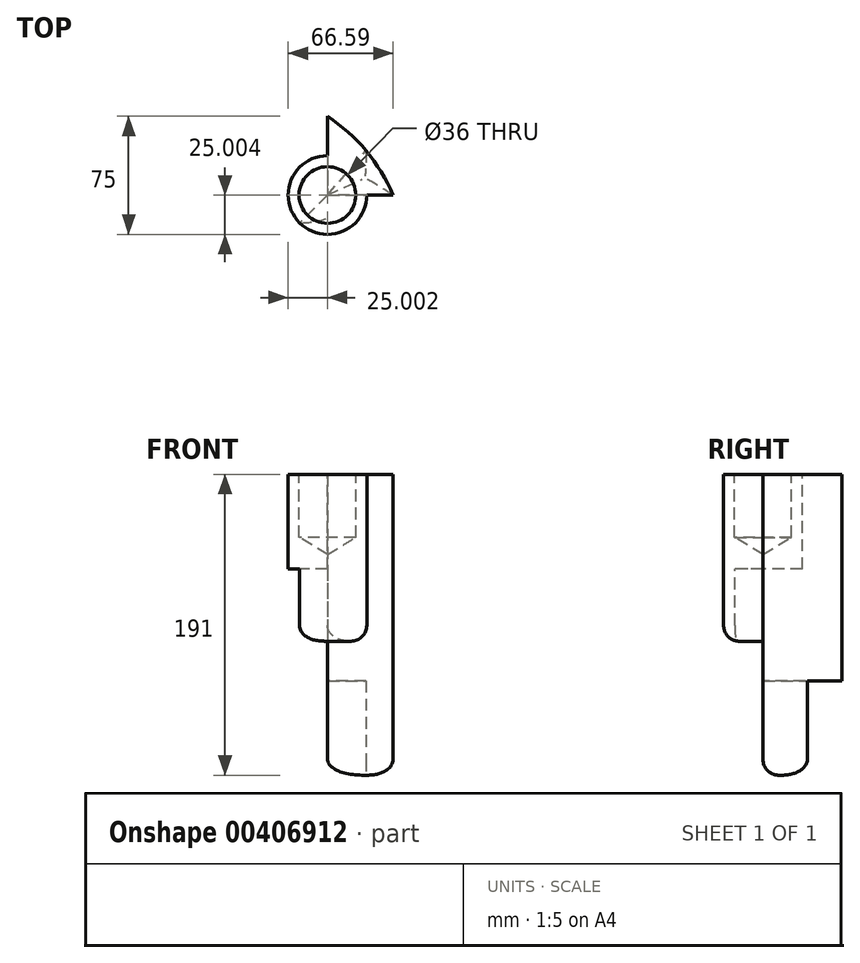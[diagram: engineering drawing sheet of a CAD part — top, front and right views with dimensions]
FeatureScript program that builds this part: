
annotation { "Feature Type Name" : "Feature", "Feature Type Description" : "" }
export const myFeature = defineFeature(function(context is Context, id is Id, definition is map)
    precondition{}
    {
        {
            var Q0;
            Q0=qCreatedBy(makeId("Top.planeOp"),FACE);
            var sketch = newSketch(context, id + "F0", { "sketchPlane" : qUnion([Q0])});
            skLineSegment(sketch, "E0.bottom", {"start": v(-15.97, 19) * mm, "end": v(34.03, 19) * mm});
            skLineSegment(sketch, "E0.top", {"start": v(-15.97, -31) * mm, "end": v(34.03, -31) * mm});
            skLineSegment(sketch, "E0.left", {"start": v(-15.97, 19) * mm, "end": v(-15.97, -31) * mm});
            skLineSegment(sketch, "E0.right", {"start": v(34.03, 19) * mm, "end": v(34.03, -31) * mm});
            skSolve(sketch);
        }
        {
            var Q0;
            Q0=makeQuery(id+"F0.imprint","IMPRINT",FACE,{"disambiguationData":[TD([[makeQuery(id+"F0.imprint","IMPRINT",EDGE,{"derivedFrom":sQuery(id+"F0.wireOp",EDGE,"E0.bottom")}),-1.0]])]});
            extrude(context, id + "F1", {"entities" : qUnion([Q0]), "depth" : 160 * mm});
        }
        {
            var Q0;
            Q0=makeQuery(id+"F1.opExtrude","SWEPT_BODY",BODY,{"disambiguationData":[OSD([sQuery(id+"F0.wireOp",EDGE,"E0.bottom"),sQuery(id+"F0.wireOp",EDGE,"E0.top"),sQuery(id+"F0.wireOp",EDGE,"E0.left"),sQuery(id+"F0.wireOp",EDGE,"E0.right")])]});
            var Q1;
            Q1=makeQuery(id+"F1.opExtrude","SWEPT_EDGE",EDGE,{"disambiguationData":[OSD([sQuery(id+"F0.wireOp",EDGE,"E0.bottom"),sQuery(id+"F0.wireOp",EDGE,"E0.left")])]});
            transform(context, id + "F2", {"entities" : qUnion([Q0]), "transformType" : TransformType.TRANSLATION_3D, "dx" : 20 * mm, "dy" : 22 * mm, "dz" : 0 * mm, "makeCopy" : false});
        }
        {
            var Q0;
            Q0=makeQuery(id+"F1.opExtrude","SWEPT_FACE",FACE,{"disambiguationData":[OSD([sQuery(id+"F0.wireOp",EDGE,"E0.top")])]});
            var sketch = newSketch(context, id + "F3", { "sketchPlane" : qUnion([Q0])});
            skLineSegment(sketch, "E1", {"start": v(4.03, 82.89) * mm, "end": v(29.03, 82.89) * mm});
            skLineSegment(sketch, "E2", {"start": v(29.03, 82.89) * mm, "end": v(29.03, 160) * mm});
            skLineSegment(sketch, "E3", {"start": v(29.03, 160) * mm, "end": v(4.03, 160) * mm});
            skLineSegment(sketch, "E4", {"start": v(4.03, 160) * mm, "end": v(4.03, 82.89) * mm});
            skSolve(sketch);
        }
        {
            var Q0;
            Q0 = qSketchRegion(id + "F3", true);
            var Q1;
            Q1=sQuery(id+"F3.wireOp",EDGE,"E4");
            revolve(context, id + "F4", {"operationType" : NewBodyOperationType.ADD, "entities" : qUnion([Q0]), "axis" : qUnion([Q1]), "revolveType" : RevolveType.FULL});
        }
        {
            var Q0;
            Q0=makeQuery(id+"F4.opRevolve","SWEPT_FACE",FACE,{"disambiguationData":[OSD([sQuery(id+"F3.wireOp",EDGE,"E1")])]});
            var sketch = newSketch(context, id + "F5", { "sketchPlane" : qUnion([Q0])});
            skLineSegment(sketch, "E5", {"start": v(4.03, 9) * mm, "end": v(-13.65, 26.67) * mm});
            skSolve(sketch);
        }
        {
            var Q0;
            Q0 = qSketchRegion(id + "F5", true);
            var Q1;
            {var subQ0=sQuery(id+"F5.wireOp",EDGE,"E5");Q1=makeQuery(id+"F5.imprint","IMPRINT",FACE,{"disambiguationData":[TD([[makeQuery(id+"F5.imprint","IMPRINT",EDGE,{"derivedFrom":subQ0}),-1.0]])]});}
            extrude(context, id + "F6", {"entities" : qUnion([Q0, Q1]), "operationType" : NewBodyOperationType.ADD, "depth" : 28.8 * mm});
        }
        {
            var Q0;
            Q0=makeQuery(id+"F4.opRevolve","SWEPT_FACE",FACE,{"disambiguationData":[OSD([sQuery(id+"F3.wireOp",EDGE,"E1")])]});
            extrude(context, id + "F7", {"entities" : qUnion([Q0]), "operationType" : NewBodyOperationType.REMOVE, "oppositeDirection" : true, "depth" : 17 * mm});
        }
        {
            var Q0;
            Q0=makeQuery(id+"F1.opExtrude","SWEPT_EDGE",EDGE,{"disambiguationData":[OSD([sQuery(id+"F0.wireOp",EDGE,"E0.bottom"),sQuery(id+"F0.wireOp",EDGE,"E0.right")])]});
            fillet(context, id + "F8", {"entities" : qUnion([Q0]), "radius" : 110 * mm, "tangentPropagation" : true, "allowEdgeOverflow" : false});
        }
        {
            var Q0;
            Q0=makeQuery(id+"F1.opExtrude","CAP_FACE",FACE,{"disambiguationData":[OSD([sQuery(id+"F0.wireOp",EDGE,"E0.bottom"),sQuery(id+"F0.wireOp",EDGE,"E0.top"),sQuery(id+"F0.wireOp",EDGE,"E0.left"),sQuery(id+"F0.wireOp",EDGE,"E0.right")])],"isStart":true});
            var sketch = newSketch(context, id + "F9", { "sketchPlane" : qUnion([Q0])});
            skLineSegment(sketch, "E6", {"start": v(4.03, 9) * mm, "end": v(28.6, -19.15) * mm});
            skSolve(sketch);
        }
        {
            var Q0;
            Q0 = qSketchRegion(id + "F9", true);
            var Q1;
            {var subQ0=sQuery(id+"F9.wireOp",EDGE,"E6");Q1=makeQuery(id+"F9.imprint","IMPRINT",FACE,{"disambiguationData":[TD([[makeQuery(id+"F9.imprint","IMPRINT",EDGE,{"derivedFrom":subQ0}),-1.0]])]});}
            extrude(context, id + "F10", {"entities" : qUnion([Q0, Q1]), "operationType" : NewBodyOperationType.REMOVE, "oppositeDirection" : true, "depth" : 29 * mm});
        }
        {
            var Q0;
            Q0=makeQuery(id+"F1.opExtrude","CAP_FACE",FACE,{"disambiguationData":[OSD([sQuery(id+"F0.wireOp",EDGE,"E0.bottom"),sQuery(id+"F0.wireOp",EDGE,"E0.top"),sQuery(id+"F0.wireOp",EDGE,"E0.left"),sQuery(id+"F0.wireOp",EDGE,"E0.right")])],"isStart":true});
            extrude(context, id + "F11", {"entities" : qUnion([Q0]), "operationType" : NewBodyOperationType.ADD, "depth" : 31 * mm});
        }
        {
            var Q0;
            Q0=makeQuery(id+"F7.boolean.opBoolean","COPY",EDGE,{"derivedFrom":makeQuery(id+"F7.opExtrude","CAP_EDGE",EDGE,{"disambiguationData":[OSD([sQuery(id+"F3.wireOp",EDGE,"E1"),sQuery(id+"F3.wireOp",EDGE,"E2")])],"isStart":false})});
            var Q1;
            Q1=makeQuery(id+"F6.opExtrude","CAP_EDGE",EDGE,{"disambiguationData":[OSD([sQuery(id+"F3.wireOp",EDGE,"E1"),sQuery(id+"F3.wireOp",EDGE,"E2")])],"isStart":false});
            var Q2;
            Q2=makeQuery(id+"F10.boolean.opBoolean","COPY",EDGE,{"derivedFrom":makeQuery(id+"F10.opExtrude","CAP_EDGE",EDGE,{"disambiguationData":[OSD([sQuery(id+"F0.wireOp",EDGE,"E0.left")])],"isStart":false})});
            var Q3;
            Q3=makeQuery(id+"F11.opExtrude","CAP_EDGE",EDGE,{"disambiguationData":[OSD([sQuery(id+"F9.wireOp",EDGE,"E6")])],"isStart":false});
            var Q4;
            Q4=makeQuery(id+"F11.opExtrude","CAP_EDGE",EDGE,{"disambiguationData":[OSD([sQuery(id+"F0.wireOp",EDGE,"E0.top")])],"isStart":false});
            var Q5;
            Q5=makeQuery(id+"F11.opExtrude","CAP_EDGE",EDGE,{"disambiguationData":[OSD([sQuery(id+"F0.wireOp",EDGE,"E0.bottom"),sQuery(id+"F0.wireOp",EDGE,"E0.top"),sQuery(id+"F0.wireOp",EDGE,"E0.left"),sQuery(id+"F0.wireOp",EDGE,"E0.right")])],"isStart":false});
            var Q6;
            Q6=makeQuery(id+"F10.boolean.opBoolean","COPY",EDGE,{"derivedFrom":makeQuery(id+"F10.opExtrude","CAP_EDGE",EDGE,{"disambiguationData":[OSD([sQuery(id+"F0.wireOp",EDGE,"E0.bottom"),sQuery(id+"F0.wireOp",EDGE,"E0.top"),sQuery(id+"F0.wireOp",EDGE,"E0.left"),sQuery(id+"F0.wireOp",EDGE,"E0.right")])],"isStart":false})});
            var Q7;
            Q7=makeQuery(id+"F6.opExtrude","CAP_EDGE",EDGE,{"disambiguationData":[OSD([sQuery(id+"F5.wireOp",EDGE,"E5")])],"isStart":false});
            fillet(context, id + "F12", {"entities" : qUnion([Q0, Q1, Q2, Q3, Q4, Q5, Q6, Q7]), "radius" : 10 * mm, "tangentPropagation" : true, "allowEdgeOverflow" : false});
        }
        {
            var Q0;
            Q0=makeQuery(id+"F4.boolean.opBoolean","MERGE",FACE,{"derivedFrom":[makeQuery(id+"F1.opExtrude","CAP_FACE",FACE,{"disambiguationData":[OSD([sQuery(id+"F0.wireOp",EDGE,"E0.bottom"),sQuery(id+"F0.wireOp",EDGE,"E0.top"),sQuery(id+"F0.wireOp",EDGE,"E0.left"),sQuery(id+"F0.wireOp",EDGE,"E0.right")])],"isStart":false}),makeQuery(id+"F4.opRevolve","SWEPT_FACE",FACE,{"disambiguationData":[OSD([sQuery(id+"F3.wireOp",EDGE,"E3")])]})]});
            var sketch = newSketch(context, id + "F13", { "sketchPlane" : qUnion([Q0])});
            skCircle(sketch, "E7", {"center": v(4.03, -9) * mm, "radius": 18 * mm});
            skSolve(sketch);
        }
        {
            var Q0;
            Q0=sQuery(id+"F13.wireOp",VERTEX,"E7.center");
            var Q1;
            Q1=makeQuery(id+"F1.opExtrude","SWEPT_BODY",BODY,{"disambiguationData":[OSD([sQuery(id+"F0.wireOp",EDGE,"E0.bottom"),sQuery(id+"F0.wireOp",EDGE,"E0.top"),sQuery(id+"F0.wireOp",EDGE,"E0.left"),sQuery(id+"F0.wireOp",EDGE,"E0.right")])]});
            hole(context, id + "F14", {"style" : HoleStyle.SIMPLE, "endStyle" : HoleEndStyle.BLIND, "holeDiameter" : 36 * mm, "holeDepth" : 40 * mm, "isTappedThrough" : true, "tappedDepth" : 12.7 * mm, "tapClearance" : 3, "locations" : qUnion([Q0]), "scope" : qUnion([Q1])});
        }
    });
